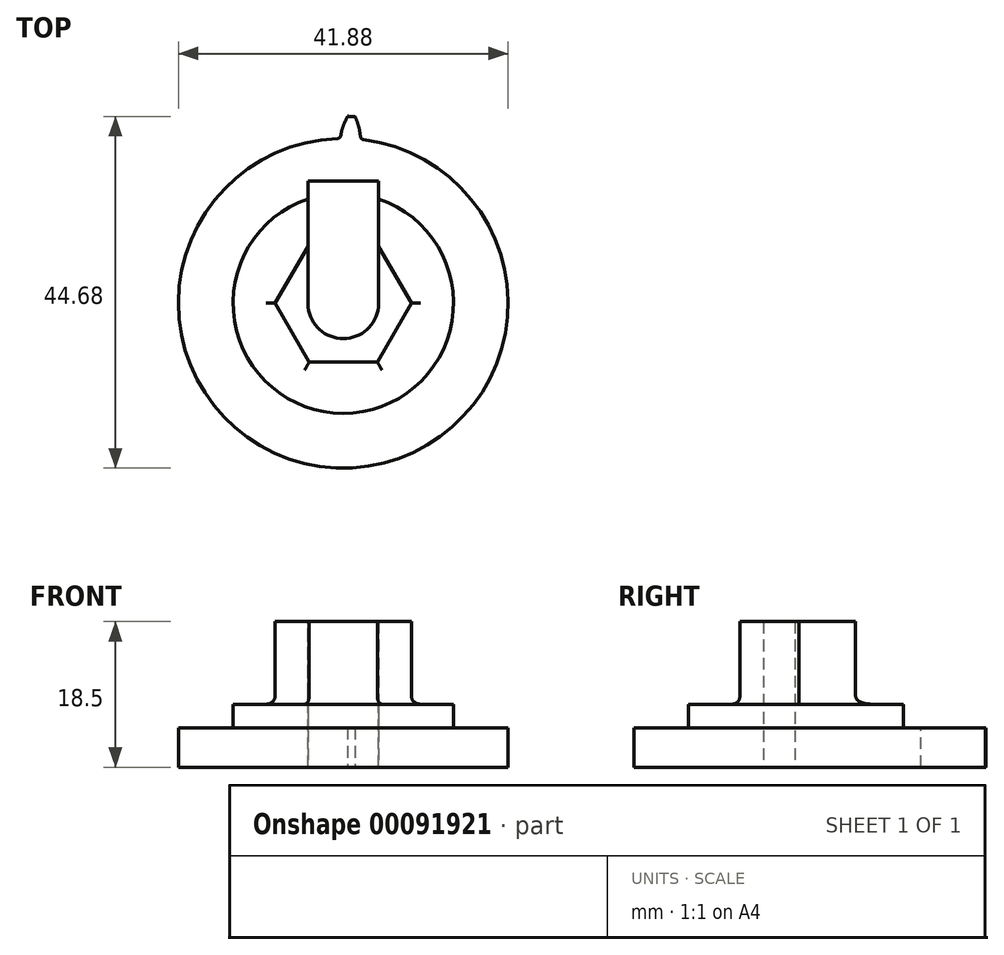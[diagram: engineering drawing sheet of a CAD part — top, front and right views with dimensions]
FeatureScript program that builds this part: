
annotation { "Feature Type Name" : "Feature", "Feature Type Description" : "" }
export const myFeature = defineFeature(function(context is Context, id is Id, definition is map)
    precondition{}
    {
        {
            var Q0;
            Q0=qCreatedBy(makeId("Front.planeOp"),FACE);
            var sketch = newSketch(context, id + "F0", { "sketchPlane" : qUnion([Q0])});
            skLineSegment(sketch, "E0", {"start": v(0, 72.27) * mm, "end": v(0, -50.25) * mm, "construction": true});
            skSolve(sketch);
        }
        {
            var Q0;
            Q0=qCreatedBy(makeId("Top.planeOp"),FACE);
            var sketch = newSketch(context, id + "F1", { "sketchPlane" : qUnion([Q0])});
            skCircle(sketch, "E1", {"center": v(0, 0) * mm, "radius": 22.5 * mm, "construction": true});
            skCircle(sketch, "E2", {"center": v(0, 0) * mm, "radius": 20.94 * mm});
            skCircle(sketch, "E3", {"center": v(0, 0) * mm, "radius": 4.5 * mm});
            skSolve(sketch);
        }
        {
            var Q0;
            Q0=qSketchRegion(id+"F1",true);
            extrude(context, id + "F2", {"entities" : qUnion([Q0]), "depth" : 5 * mm});
        }
        {
            var Q0;
            Q0=qCreatedBy(makeId("Top.planeOp"),FACE);
            var sketch = newSketch(context, id + "F3", { "sketchPlane" : qUnion([Q0])});
            skLineSegment(sketch, "E4", {"start": v(0, 0) * mm, "end": v(0, 29.7) * mm, "construction": true});
            skLineSegment(sketch, "E5", {"start": v(0, 0) * mm, "end": v(-10.47, 28.76) * mm, "construction": true});
            skLineSegment(sketch, "E6", {"start": v(0, 22.5) * mm, "end": v(-7.23, 19.87) * mm, "construction": true});
            skCircle(sketch, "E7", {"center": v(0, 0) * mm, "radius": 22.5 * mm, "construction": true});
            skCircle(sketch, "E8", {"center": v(0, 0) * mm, "radius": 23.75 * mm, "construction": true});
            skArc(sketch, "E9", {"start": v(-0.76, 20.92) * mm, "mid": v(-0.91, -20.92) * mm, "end": v(2.58, 20.78) * mm, "construction": true});
            skCircle(sketch, "E10", {"center": v(0, 0) * mm, "radius": 21.14 * mm, "construction": true});
            skCircle(sketch, "E11", {"center": v(8.83, 19.21) * mm, "radius": 9.42 * mm, "construction": true});
            skCircle(sketch, "E12", {"center": v(5.74, 20.35) * mm, "radius": 6.13 * mm, "construction": true});
            skArc(sketch, "E13", {"start": v(0.57, 23.74) * mm, "mid": v(0.26, 23.13) * mm, "end": v(0, 22.5) * mm});
            skArc(sketch, "E14", {"start": v(0, 22.5) * mm, "mid": v(-0.2, 21.83) * mm, "end": v(-0.34, 21.14) * mm});
            skArc(sketch, "E15", {"start": v(1.96, 22.41) * mm, "mid": v(0.98, 22.48) * mm, "end": v(0, 22.5) * mm});
            skLineSegment(sketch, "E16", {"start": v(0, 0) * mm, "end": v(0.98, 22.48) * mm, "construction": true});
            skLineSegment(sketch, "E17", {"start": v(0.56, 12.86) * mm, "end": v(0.98, 22.48) * mm, "construction": true});
            skArc(sketch, "E18", {"start": v(1.04, 23.73) * mm, "mid": v(0.8, 23.74) * mm, "end": v(0.57, 23.74) * mm});
            skArc(sketch, "E19.MirrorCS", {"start": v(1.04, 23.73) * mm, "mid": v(1.27, 23.72) * mm, "end": v(1.5, 23.7) * mm});
            skArc(sketch, "E20.MirrorCS", {"start": v(1.5, 23.7) * mm, "mid": v(1.76, 23.07) * mm, "end": v(1.96, 22.41) * mm});
            skArc(sketch, "E21.MirrorCS", {"start": v(1.96, 22.41) * mm, "mid": v(2.11, 21.73) * mm, "end": v(2.18, 21.03) * mm});
            skArc(sketch, "E22.filletArc", {"start": v(-0.76, 20.92) * mm, "mid": v(-0.47, 21.04) * mm, "end": v(-0.31, 21.32) * mm});
            skArc(sketch, "E23.MirrorCS", {"start": v(2.58, 20.78) * mm, "mid": v(2.3, 20.92) * mm, "end": v(2.17, 21.2) * mm});
            skArc(sketch, "E24", {"start": v(-0.76, 20.92) * mm, "mid": v(0.91, 20.92) * mm, "end": v(2.58, 20.78) * mm});
            skSolve(sketch);
        }
        {
            var Q0;
            Q0=qSketchRegion(id+"F3",true);
            extrude(context, id + "F4", {"entities" : qUnion([Q0]), "operationType" : NewBodyOperationType.ADD, "depth" : 5 * mm});
        }
        {
            var Q0;
            {var subQ0=sQuery(id+"F3.wireOp",EDGE,"E24");var subQ1=sQuery(id+"F3.wireOp",EDGE,"E23.MirrorCS");var subQ2=sQuery(id+"F3.wireOp",EDGE,"E22.filletArc");var subQ3=sQuery(id+"F3.wireOp",EDGE,"78956dcd-a33f-4312-9058-d5f61c118e150.MirrorCS");var subQ4=sQuery(id+"F3.wireOp",EDGE,"E21.MirrorCS");var subQ5=sQuery(id+"F3.wireOp",EDGE,"E20.MirrorCS");var subQ6=sQuery(id+"F3.wireOp",EDGE,"E19.MirrorCS");var subQ7=sQuery(id+"F3.wireOp",EDGE,"E18");var subQ8=sQuery(id+"F3.wireOp",EDGE,"4TcJw9v4-HVDb-vTLw-8M1V-rvmi7eCVJvvU");var subQ9=sQuery(id+"F3.wireOp",EDGE,"E14");var subQ10=sQuery(id+"F3.wireOp",EDGE,"E13");Q0=makeQuery(id+"FKo0gFQ4KOUnKrD_1.29.F4.boolean.opBoolean","MERGE",FACE,{"derivedFrom":[makeQuery(id+"FKo0gFQ4KOUnKrD_1.28.F4.boolean.opBoolean","MERGE",FACE,{"derivedFrom":[makeQuery(id+"FKo0gFQ4KOUnKrD_1.27.F4.boolean.opBoolean","MERGE",FACE,{"derivedFrom":[makeQuery(id+"FKo0gFQ4KOUnKrD_1.26.F4.boolean.opBoolean","MERGE",FACE,{"derivedFrom":[makeQuery(id+"FKo0gFQ4KOUnKrD_1.25.F4.boolean.opBoolean","MERGE",FACE,{"derivedFrom":[makeQuery(id+"FKo0gFQ4KOUnKrD_1.24.F4.boolean.opBoolean","MERGE",FACE,{"derivedFrom":[makeQuery(id+"FKo0gFQ4KOUnKrD_1.23.F4.boolean.opBoolean","MERGE",FACE,{"derivedFrom":[makeQuery(id+"FKo0gFQ4KOUnKrD_1.22.F4.boolean.opBoolean","MERGE",FACE,{"derivedFrom":[makeQuery(id+"FKo0gFQ4KOUnKrD_1.21.F4.boolean.opBoolean","MERGE",FACE,{"derivedFrom":[makeQuery(id+"FKo0gFQ4KOUnKrD_1.20.F4.boolean.opBoolean","MERGE",FACE,{"derivedFrom":[makeQuery(id+"FKo0gFQ4KOUnKrD_1.19.F4.boolean.opBoolean","MERGE",FACE,{"derivedFrom":[makeQuery(id+"FKo0gFQ4KOUnKrD_1.18.F4.boolean.opBoolean","MERGE",FACE,{"derivedFrom":[makeQuery(id+"FKo0gFQ4KOUnKrD_1.17.F4.boolean.opBoolean","MERGE",FACE,{"derivedFrom":[makeQuery(id+"FKo0gFQ4KOUnKrD_1.16.F4.boolean.opBoolean","MERGE",FACE,{"derivedFrom":[makeQuery(id+"FKo0gFQ4KOUnKrD_1.15.F4.boolean.opBoolean","MERGE",FACE,{"derivedFrom":[makeQuery(id+"FKo0gFQ4KOUnKrD_1.14.F4.boolean.opBoolean","MERGE",FACE,{"derivedFrom":[makeQuery(id+"FKo0gFQ4KOUnKrD_1.13.F4.boolean.opBoolean","MERGE",FACE,{"derivedFrom":[makeQuery(id+"FKo0gFQ4KOUnKrD_1.12.F4.boolean.opBoolean","MERGE",FACE,{"derivedFrom":[makeQuery(id+"FKo0gFQ4KOUnKrD_1.11.F4.boolean.opBoolean","MERGE",FACE,{"derivedFrom":[makeQuery(id+"FKo0gFQ4KOUnKrD_1.10.F4.boolean.opBoolean","MERGE",FACE,{"derivedFrom":[makeQuery(id+"FKo0gFQ4KOUnKrD_1.9.F4.boolean.opBoolean","MERGE",FACE,{"derivedFrom":[makeQuery(id+"FKo0gFQ4KOUnKrD_1.8.F4.boolean.opBoolean","MERGE",FACE,{"derivedFrom":[makeQuery(id+"FKo0gFQ4KOUnKrD_1.7.F4.boolean.opBoolean","MERGE",FACE,{"derivedFrom":[makeQuery(id+"FKo0gFQ4KOUnKrD_1.6.F4.boolean.opBoolean","MERGE",FACE,{"derivedFrom":[makeQuery(id+"FKo0gFQ4KOUnKrD_1.5.F4.boolean.opBoolean","MERGE",FACE,{"derivedFrom":[makeQuery(id+"FKo0gFQ4KOUnKrD_1.4.F4.boolean.opBoolean","MERGE",FACE,{"derivedFrom":[makeQuery(id+"FKo0gFQ4KOUnKrD_1.3.F4.boolean.opBoolean","MERGE",FACE,{"derivedFrom":[makeQuery(id+"FKo0gFQ4KOUnKrD_1.2.F4.boolean.opBoolean","MERGE",FACE,{"derivedFrom":[makeQuery(id+"FKo0gFQ4KOUnKrD_1.1.F4.boolean.opBoolean","MERGE",FACE,{"derivedFrom":[makeQuery(id+"F4.boolean.opBoolean","MERGE",FACE,{"derivedFrom":[makeQuery(id+"F2.opExtrude","CAP_FACE",FACE,{"disambiguationData":[OSD([sQuery(id+"F1.wireOp",EDGE,"E2"),sQuery(id+"F1.wireOp",EDGE,"E3")])],"isStart":false}),makeQuery(id+"F4.opExtrude","CAP_FACE",FACE,{"disambiguationData":[OSD([subQ10,subQ9,subQ8,subQ7,subQ6,subQ5,subQ4,subQ3,subQ2,subQ1,subQ0])],"isStart":false})]}),makeQuery(id+"FKo0gFQ4KOUnKrD_1.1.F4.opExtrude","CAP_FACE",FACE,{"disambiguationData":[OSD([subQ10,subQ9,subQ8,subQ7,subQ6,subQ5,subQ4,subQ3,subQ2,subQ1,subQ0])],"isStart":false})]}),makeQuery(id+"FKo0gFQ4KOUnKrD_1.2.F4.opExtrude","CAP_FACE",FACE,{"disambiguationData":[OSD([subQ10,subQ9,subQ8,subQ7,subQ6,subQ5,subQ4,subQ3,subQ2,subQ1,subQ0])],"isStart":false})]}),makeQuery(id+"FKo0gFQ4KOUnKrD_1.3.F4.opExtrude","CAP_FACE",FACE,{"disambiguationData":[OSD([subQ10,subQ9,subQ8,subQ7,subQ6,subQ5,subQ4,subQ3,subQ2,subQ1,subQ0])],"isStart":false})]}),makeQuery(id+"FKo0gFQ4KOUnKrD_1.4.F4.opExtrude","CAP_FACE",FACE,{"disambiguationData":[OSD([subQ10,subQ9,subQ8,subQ7,subQ6,subQ5,subQ4,subQ3,subQ2,subQ1,subQ0])],"isStart":false})]}),makeQuery(id+"FKo0gFQ4KOUnKrD_1.5.F4.opExtrude","CAP_FACE",FACE,{"disambiguationData":[OSD([subQ10,subQ9,subQ8,subQ7,subQ6,subQ5,subQ4,subQ3,subQ2,subQ1,subQ0])],"isStart":false})]}),makeQuery(id+"FKo0gFQ4KOUnKrD_1.6.F4.opExtrude","CAP_FACE",FACE,{"disambiguationData":[OSD([subQ10,subQ9,subQ8,subQ7,subQ6,subQ5,subQ4,subQ3,subQ2,subQ1,subQ0])],"isStart":false})]}),makeQuery(id+"FKo0gFQ4KOUnKrD_1.7.F4.opExtrude","CAP_FACE",FACE,{"disambiguationData":[OSD([subQ10,subQ9,subQ8,subQ7,subQ6,subQ5,subQ4,subQ3,subQ2,subQ1,subQ0])],"isStart":false})]}),makeQuery(id+"FKo0gFQ4KOUnKrD_1.8.F4.opExtrude","CAP_FACE",FACE,{"disambiguationData":[OSD([subQ10,subQ9,subQ8,subQ7,subQ6,subQ5,subQ4,subQ3,subQ2,subQ1,subQ0])],"isStart":false})]}),makeQuery(id+"FKo0gFQ4KOUnKrD_1.9.F4.opExtrude","CAP_FACE",FACE,{"disambiguationData":[OSD([subQ10,subQ9,subQ8,subQ7,subQ6,subQ5,subQ4,subQ3,subQ2,subQ1,subQ0])],"isStart":false})]}),makeQuery(id+"FKo0gFQ4KOUnKrD_1.10.F4.opExtrude","CAP_FACE",FACE,{"disambiguationData":[OSD([subQ10,subQ9,subQ8,subQ7,subQ6,subQ5,subQ4,subQ3,subQ2,subQ1,subQ0])],"isStart":false})]}),makeQuery(id+"FKo0gFQ4KOUnKrD_1.11.F4.opExtrude","CAP_FACE",FACE,{"disambiguationData":[OSD([subQ10,subQ9,subQ8,subQ7,subQ6,subQ5,subQ4,subQ3,subQ2,subQ1,subQ0])],"isStart":false})]}),makeQuery(id+"FKo0gFQ4KOUnKrD_1.12.F4.opExtrude","CAP_FACE",FACE,{"disambiguationData":[OSD([subQ10,subQ9,subQ8,subQ7,subQ6,subQ5,subQ4,subQ3,subQ2,subQ1,subQ0])],"isStart":false})]}),makeQuery(id+"FKo0gFQ4KOUnKrD_1.13.F4.opExtrude","CAP_FACE",FACE,{"disambiguationData":[OSD([subQ10,subQ9,subQ8,subQ7,subQ6,subQ5,subQ4,subQ3,subQ2,subQ1,subQ0])],"isStart":false})]}),makeQuery(id+"FKo0gFQ4KOUnKrD_1.14.F4.opExtrude","CAP_FACE",FACE,{"disambiguationData":[OSD([subQ10,subQ9,subQ8,subQ7,subQ6,subQ5,subQ4,subQ3,subQ2,subQ1,subQ0])],"isStart":false})]}),makeQuery(id+"FKo0gFQ4KOUnKrD_1.15.F4.opExtrude","CAP_FACE",FACE,{"disambiguationData":[OSD([subQ10,subQ9,subQ8,subQ7,subQ6,subQ5,subQ4,subQ3,subQ2,subQ1,subQ0])],"isStart":false})]}),makeQuery(id+"FKo0gFQ4KOUnKrD_1.16.F4.opExtrude","CAP_FACE",FACE,{"disambiguationData":[OSD([subQ10,subQ9,subQ8,subQ7,subQ6,subQ5,subQ4,subQ3,subQ2,subQ1,subQ0])],"isStart":false})]}),makeQuery(id+"FKo0gFQ4KOUnKrD_1.17.F4.opExtrude","CAP_FACE",FACE,{"disambiguationData":[OSD([subQ10,subQ9,subQ8,subQ7,subQ6,subQ5,subQ4,subQ3,subQ2,subQ1,subQ0])],"isStart":false})]}),makeQuery(id+"FKo0gFQ4KOUnKrD_1.18.F4.opExtrude","CAP_FACE",FACE,{"disambiguationData":[OSD([subQ10,subQ9,subQ8,subQ7,subQ6,subQ5,subQ4,subQ3,subQ2,subQ1,subQ0])],"isStart":false})]}),makeQuery(id+"FKo0gFQ4KOUnKrD_1.19.F4.opExtrude","CAP_FACE",FACE,{"disambiguationData":[OSD([subQ10,subQ9,subQ8,subQ7,subQ6,subQ5,subQ4,subQ3,subQ2,subQ1,subQ0])],"isStart":false})]}),makeQuery(id+"FKo0gFQ4KOUnKrD_1.20.F4.opExtrude","CAP_FACE",FACE,{"disambiguationData":[OSD([subQ10,subQ9,subQ8,subQ7,subQ6,subQ5,subQ4,subQ3,subQ2,subQ1,subQ0])],"isStart":false})]}),makeQuery(id+"FKo0gFQ4KOUnKrD_1.21.F4.opExtrude","CAP_FACE",FACE,{"disambiguationData":[OSD([subQ10,subQ9,subQ8,subQ7,subQ6,subQ5,subQ4,subQ3,subQ2,subQ1,subQ0])],"isStart":false})]}),makeQuery(id+"FKo0gFQ4KOUnKrD_1.22.F4.opExtrude","CAP_FACE",FACE,{"disambiguationData":[OSD([subQ10,subQ9,subQ8,subQ7,subQ6,subQ5,subQ4,subQ3,subQ2,subQ1,subQ0])],"isStart":false})]}),makeQuery(id+"FKo0gFQ4KOUnKrD_1.23.F4.opExtrude","CAP_FACE",FACE,{"disambiguationData":[OSD([subQ10,subQ9,subQ8,subQ7,subQ6,subQ5,subQ4,subQ3,subQ2,subQ1,subQ0])],"isStart":false})]}),makeQuery(id+"FKo0gFQ4KOUnKrD_1.24.F4.opExtrude","CAP_FACE",FACE,{"disambiguationData":[OSD([subQ10,subQ9,subQ8,subQ7,subQ6,subQ5,subQ4,subQ3,subQ2,subQ1,subQ0])],"isStart":false})]}),makeQuery(id+"FKo0gFQ4KOUnKrD_1.25.F4.opExtrude","CAP_FACE",FACE,{"disambiguationData":[OSD([subQ10,subQ9,subQ8,subQ7,subQ6,subQ5,subQ4,subQ3,subQ2,subQ1,subQ0])],"isStart":false})]}),makeQuery(id+"FKo0gFQ4KOUnKrD_1.26.F4.opExtrude","CAP_FACE",FACE,{"disambiguationData":[OSD([subQ10,subQ9,subQ8,subQ7,subQ6,subQ5,subQ4,subQ3,subQ2,subQ1,subQ0])],"isStart":false})]}),makeQuery(id+"FKo0gFQ4KOUnKrD_1.27.F4.opExtrude","CAP_FACE",FACE,{"disambiguationData":[OSD([subQ10,subQ9,subQ8,subQ7,subQ6,subQ5,subQ4,subQ3,subQ2,subQ1,subQ0])],"isStart":false})]}),makeQuery(id+"FKo0gFQ4KOUnKrD_1.28.F4.opExtrude","CAP_FACE",FACE,{"disambiguationData":[OSD([subQ10,subQ9,subQ8,subQ7,subQ6,subQ5,subQ4,subQ3,subQ2,subQ1,subQ0])],"isStart":false})]}),makeQuery(id+"FKo0gFQ4KOUnKrD_1.29.F4.opExtrude","CAP_FACE",FACE,{"disambiguationData":[OSD([subQ10,subQ9,subQ8,subQ7,subQ6,subQ5,subQ4,subQ3,subQ2,subQ1,subQ0])],"isStart":false})]});}
            var sketch = newSketch(context, id + "F5", { "sketchPlane" : qUnion([Q0])});
            skCircle(sketch, "E25.cCircle", {"center": v(0, 0) * mm, "radius": 7.5 * mm, "construction": true});
            skLineSegment(sketch, "E25.0", {"start": v(4.33, 7.5) * mm, "end": v(8.66, 0) * mm});
            skLineSegment(sketch, "E25.1", {"start": v(8.66, 0) * mm, "end": v(4.33, -7.5) * mm});
            skLineSegment(sketch, "E25.2", {"start": v(4.33, -7.5) * mm, "end": v(-4.33, -7.5) * mm});
            skLineSegment(sketch, "E25.3", {"start": v(-4.33, -7.5) * mm, "end": v(-8.66, 0) * mm});
            skLineSegment(sketch, "E25.4", {"start": v(-8.66, 0) * mm, "end": v(-4.33, 7.5) * mm});
            skLineSegment(sketch, "E25.5", {"start": v(-4.33, 7.5) * mm, "end": v(4.33, 7.5) * mm});
            skPoint(sketch, "E25.0.midPoint", {"position": v(6.5, 3.75) * mm});
            skCircle(sketch, "E26.0", {"center": v(0, 0) * mm, "radius": 4.5 * mm});
            skSolve(sketch);
        }
        {
            var Q0;
            Q0 = qSketchRegion(id + "F5", true);
            extrude(context, id + "F6", {"entities" : qUnion([Q0]), "operationType" : NewBodyOperationType.ADD, "depth" : 13.5 * mm});
        }
        {
            var Q0;
            {var subQ0=sQuery(id+"F3.wireOp",EDGE,"E24");var subQ1=sQuery(id+"F3.wireOp",EDGE,"E23.MirrorCS");var subQ2=sQuery(id+"F3.wireOp",EDGE,"E22.filletArc");var subQ3=sQuery(id+"F3.wireOp",EDGE,"E21.MirrorCS");var subQ4=sQuery(id+"F3.wireOp",EDGE,"E20.MirrorCS");var subQ5=sQuery(id+"F3.wireOp",EDGE,"E19.MirrorCS");var subQ6=sQuery(id+"F3.wireOp",EDGE,"E18");var subQ7=sQuery(id+"F3.wireOp",EDGE,"E14");var subQ8=sQuery(id+"F3.wireOp",EDGE,"E13");Q0=makeQuery(id+"FKo0gFQ4KOUnKrD_1.35.F4.boolean.opBoolean","MERGE",FACE,{"derivedFrom":[makeQuery(id+"FKo0gFQ4KOUnKrD_1.34.F4.boolean.opBoolean","MERGE",FACE,{"derivedFrom":[makeQuery(id+"FKo0gFQ4KOUnKrD_1.33.F4.boolean.opBoolean","MERGE",FACE,{"derivedFrom":[makeQuery(id+"FKo0gFQ4KOUnKrD_1.32.F4.boolean.opBoolean","MERGE",FACE,{"derivedFrom":[makeQuery(id+"FKo0gFQ4KOUnKrD_1.31.F4.boolean.opBoolean","MERGE",FACE,{"derivedFrom":[makeQuery(id+"FKo0gFQ4KOUnKrD_1.30.F4.boolean.opBoolean","MERGE",FACE,{"derivedFrom":[makeQuery(id+"FKo0gFQ4KOUnKrD_1.29.F4.boolean.opBoolean","MERGE",FACE,{"derivedFrom":[makeQuery(id+"FKo0gFQ4KOUnKrD_1.28.F4.boolean.opBoolean","MERGE",FACE,{"derivedFrom":[makeQuery(id+"FKo0gFQ4KOUnKrD_1.27.F4.boolean.opBoolean","MERGE",FACE,{"derivedFrom":[makeQuery(id+"FKo0gFQ4KOUnKrD_1.26.F4.boolean.opBoolean","MERGE",FACE,{"derivedFrom":[makeQuery(id+"FKo0gFQ4KOUnKrD_1.25.F4.boolean.opBoolean","MERGE",FACE,{"derivedFrom":[makeQuery(id+"FKo0gFQ4KOUnKrD_1.24.F4.boolean.opBoolean","MERGE",FACE,{"derivedFrom":[makeQuery(id+"FKo0gFQ4KOUnKrD_1.23.F4.boolean.opBoolean","MERGE",FACE,{"derivedFrom":[makeQuery(id+"FKo0gFQ4KOUnKrD_1.22.F4.boolean.opBoolean","MERGE",FACE,{"derivedFrom":[makeQuery(id+"FKo0gFQ4KOUnKrD_1.21.F4.boolean.opBoolean","MERGE",FACE,{"derivedFrom":[makeQuery(id+"FKo0gFQ4KOUnKrD_1.20.F4.boolean.opBoolean","MERGE",FACE,{"derivedFrom":[makeQuery(id+"FKo0gFQ4KOUnKrD_1.19.F4.boolean.opBoolean","MERGE",FACE,{"derivedFrom":[makeQuery(id+"FKo0gFQ4KOUnKrD_1.18.F4.boolean.opBoolean","MERGE",FACE,{"derivedFrom":[makeQuery(id+"FKo0gFQ4KOUnKrD_1.17.F4.boolean.opBoolean","MERGE",FACE,{"derivedFrom":[makeQuery(id+"FKo0gFQ4KOUnKrD_1.16.F4.boolean.opBoolean","MERGE",FACE,{"derivedFrom":[makeQuery(id+"FKo0gFQ4KOUnKrD_1.15.F4.boolean.opBoolean","MERGE",FACE,{"derivedFrom":[makeQuery(id+"FKo0gFQ4KOUnKrD_1.14.F4.boolean.opBoolean","MERGE",FACE,{"derivedFrom":[makeQuery(id+"FKo0gFQ4KOUnKrD_1.13.F4.boolean.opBoolean","MERGE",FACE,{"derivedFrom":[makeQuery(id+"FKo0gFQ4KOUnKrD_1.12.F4.boolean.opBoolean","MERGE",FACE,{"derivedFrom":[makeQuery(id+"FKo0gFQ4KOUnKrD_1.11.F4.boolean.opBoolean","MERGE",FACE,{"derivedFrom":[makeQuery(id+"FKo0gFQ4KOUnKrD_1.10.F4.boolean.opBoolean","MERGE",FACE,{"derivedFrom":[makeQuery(id+"FKo0gFQ4KOUnKrD_1.9.F4.boolean.opBoolean","MERGE",FACE,{"derivedFrom":[makeQuery(id+"FKo0gFQ4KOUnKrD_1.8.F4.boolean.opBoolean","MERGE",FACE,{"derivedFrom":[makeQuery(id+"FKo0gFQ4KOUnKrD_1.7.F4.boolean.opBoolean","MERGE",FACE,{"derivedFrom":[makeQuery(id+"FKo0gFQ4KOUnKrD_1.6.F4.boolean.opBoolean","MERGE",FACE,{"derivedFrom":[makeQuery(id+"FKo0gFQ4KOUnKrD_1.5.F4.boolean.opBoolean","MERGE",FACE,{"derivedFrom":[makeQuery(id+"FKo0gFQ4KOUnKrD_1.4.F4.boolean.opBoolean","MERGE",FACE,{"derivedFrom":[makeQuery(id+"FKo0gFQ4KOUnKrD_1.3.F4.boolean.opBoolean","MERGE",FACE,{"derivedFrom":[makeQuery(id+"FKo0gFQ4KOUnKrD_1.2.F4.boolean.opBoolean","MERGE",FACE,{"derivedFrom":[makeQuery(id+"FKo0gFQ4KOUnKrD_1.1.F4.boolean.opBoolean","MERGE",FACE,{"derivedFrom":[makeQuery(id+"F4.boolean.opBoolean","MERGE",FACE,{"derivedFrom":[makeQuery(id+"F2.opExtrude","CAP_FACE",FACE,{"disambiguationData":[OSD([sQuery(id+"F1.wireOp",EDGE,"E2"),sQuery(id+"F1.wireOp",EDGE,"E3")])],"isStart":false}),makeQuery(id+"F4.opExtrude","CAP_FACE",FACE,{"disambiguationData":[OSD([subQ8,subQ7,subQ6,subQ5,subQ4,subQ3,subQ2,subQ1,subQ0])],"isStart":false})]}),makeQuery(id+"FKo0gFQ4KOUnKrD_1.1.F4.opExtrude","CAP_FACE",FACE,{"disambiguationData":[OSD([subQ8,subQ7,subQ6,subQ5,subQ4,subQ3,subQ2,subQ1,subQ0])],"isStart":false})]}),makeQuery(id+"FKo0gFQ4KOUnKrD_1.2.F4.opExtrude","CAP_FACE",FACE,{"disambiguationData":[OSD([subQ8,subQ7,subQ6,subQ5,subQ4,subQ3,subQ2,subQ1,subQ0])],"isStart":false})]}),makeQuery(id+"FKo0gFQ4KOUnKrD_1.3.F4.opExtrude","CAP_FACE",FACE,{"disambiguationData":[OSD([subQ8,subQ7,subQ6,subQ5,subQ4,subQ3,subQ2,subQ1,subQ0])],"isStart":false})]}),makeQuery(id+"FKo0gFQ4KOUnKrD_1.4.F4.opExtrude","CAP_FACE",FACE,{"disambiguationData":[OSD([subQ8,subQ7,subQ6,subQ5,subQ4,subQ3,subQ2,subQ1,subQ0])],"isStart":false})]}),makeQuery(id+"FKo0gFQ4KOUnKrD_1.5.F4.opExtrude","CAP_FACE",FACE,{"disambiguationData":[OSD([subQ8,subQ7,subQ6,subQ5,subQ4,subQ3,subQ2,subQ1,subQ0])],"isStart":false})]}),makeQuery(id+"FKo0gFQ4KOUnKrD_1.6.F4.opExtrude","CAP_FACE",FACE,{"disambiguationData":[OSD([subQ8,subQ7,subQ6,subQ5,subQ4,subQ3,subQ2,subQ1,subQ0])],"isStart":false})]}),makeQuery(id+"FKo0gFQ4KOUnKrD_1.7.F4.opExtrude","CAP_FACE",FACE,{"disambiguationData":[OSD([subQ8,subQ7,subQ6,subQ5,subQ4,subQ3,subQ2,subQ1,subQ0])],"isStart":false})]}),makeQuery(id+"FKo0gFQ4KOUnKrD_1.8.F4.opExtrude","CAP_FACE",FACE,{"disambiguationData":[OSD([subQ8,subQ7,subQ6,subQ5,subQ4,subQ3,subQ2,subQ1,subQ0])],"isStart":false})]}),makeQuery(id+"FKo0gFQ4KOUnKrD_1.9.F4.opExtrude","CAP_FACE",FACE,{"disambiguationData":[OSD([subQ8,subQ7,subQ6,subQ5,subQ4,subQ3,subQ2,subQ1,subQ0])],"isStart":false})]}),makeQuery(id+"FKo0gFQ4KOUnKrD_1.10.F4.opExtrude","CAP_FACE",FACE,{"disambiguationData":[OSD([subQ8,subQ7,subQ6,subQ5,subQ4,subQ3,subQ2,subQ1,subQ0])],"isStart":false})]}),makeQuery(id+"FKo0gFQ4KOUnKrD_1.11.F4.opExtrude","CAP_FACE",FACE,{"disambiguationData":[OSD([subQ8,subQ7,subQ6,subQ5,subQ4,subQ3,subQ2,subQ1,subQ0])],"isStart":false})]}),makeQuery(id+"FKo0gFQ4KOUnKrD_1.12.F4.opExtrude","CAP_FACE",FACE,{"disambiguationData":[OSD([subQ8,subQ7,subQ6,subQ5,subQ4,subQ3,subQ2,subQ1,subQ0])],"isStart":false})]}),makeQuery(id+"FKo0gFQ4KOUnKrD_1.13.F4.opExtrude","CAP_FACE",FACE,{"disambiguationData":[OSD([subQ8,subQ7,subQ6,subQ5,subQ4,subQ3,subQ2,subQ1,subQ0])],"isStart":false})]}),makeQuery(id+"FKo0gFQ4KOUnKrD_1.14.F4.opExtrude","CAP_FACE",FACE,{"disambiguationData":[OSD([subQ8,subQ7,subQ6,subQ5,subQ4,subQ3,subQ2,subQ1,subQ0])],"isStart":false})]}),makeQuery(id+"FKo0gFQ4KOUnKrD_1.15.F4.opExtrude","CAP_FACE",FACE,{"disambiguationData":[OSD([subQ8,subQ7,subQ6,subQ5,subQ4,subQ3,subQ2,subQ1,subQ0])],"isStart":false})]}),makeQuery(id+"FKo0gFQ4KOUnKrD_1.16.F4.opExtrude","CAP_FACE",FACE,{"disambiguationData":[OSD([subQ8,subQ7,subQ6,subQ5,subQ4,subQ3,subQ2,subQ1,subQ0])],"isStart":false})]}),makeQuery(id+"FKo0gFQ4KOUnKrD_1.17.F4.opExtrude","CAP_FACE",FACE,{"disambiguationData":[OSD([subQ8,subQ7,subQ6,subQ5,subQ4,subQ3,subQ2,subQ1,subQ0])],"isStart":false})]}),makeQuery(id+"FKo0gFQ4KOUnKrD_1.18.F4.opExtrude","CAP_FACE",FACE,{"disambiguationData":[OSD([subQ8,subQ7,subQ6,subQ5,subQ4,subQ3,subQ2,subQ1,subQ0])],"isStart":false})]}),makeQuery(id+"FKo0gFQ4KOUnKrD_1.19.F4.opExtrude","CAP_FACE",FACE,{"disambiguationData":[OSD([subQ8,subQ7,subQ6,subQ5,subQ4,subQ3,subQ2,subQ1,subQ0])],"isStart":false})]}),makeQuery(id+"FKo0gFQ4KOUnKrD_1.20.F4.opExtrude","CAP_FACE",FACE,{"disambiguationData":[OSD([subQ8,subQ7,subQ6,subQ5,subQ4,subQ3,subQ2,subQ1,subQ0])],"isStart":false})]}),makeQuery(id+"FKo0gFQ4KOUnKrD_1.21.F4.opExtrude","CAP_FACE",FACE,{"disambiguationData":[OSD([subQ8,subQ7,subQ6,subQ5,subQ4,subQ3,subQ2,subQ1,subQ0])],"isStart":false})]}),makeQuery(id+"FKo0gFQ4KOUnKrD_1.22.F4.opExtrude","CAP_FACE",FACE,{"disambiguationData":[OSD([subQ8,subQ7,subQ6,subQ5,subQ4,subQ3,subQ2,subQ1,subQ0])],"isStart":false})]}),makeQuery(id+"FKo0gFQ4KOUnKrD_1.23.F4.opExtrude","CAP_FACE",FACE,{"disambiguationData":[OSD([subQ8,subQ7,subQ6,subQ5,subQ4,subQ3,subQ2,subQ1,subQ0])],"isStart":false})]}),makeQuery(id+"FKo0gFQ4KOUnKrD_1.24.F4.opExtrude","CAP_FACE",FACE,{"disambiguationData":[OSD([subQ8,subQ7,subQ6,subQ5,subQ4,subQ3,subQ2,subQ1,subQ0])],"isStart":false})]}),makeQuery(id+"FKo0gFQ4KOUnKrD_1.25.F4.opExtrude","CAP_FACE",FACE,{"disambiguationData":[OSD([subQ8,subQ7,subQ6,subQ5,subQ4,subQ3,subQ2,subQ1,subQ0])],"isStart":false})]}),makeQuery(id+"FKo0gFQ4KOUnKrD_1.26.F4.opExtrude","CAP_FACE",FACE,{"disambiguationData":[OSD([subQ8,subQ7,subQ6,subQ5,subQ4,subQ3,subQ2,subQ1,subQ0])],"isStart":false})]}),makeQuery(id+"FKo0gFQ4KOUnKrD_1.27.F4.opExtrude","CAP_FACE",FACE,{"disambiguationData":[OSD([subQ8,subQ7,subQ6,subQ5,subQ4,subQ3,subQ2,subQ1,subQ0])],"isStart":false})]}),makeQuery(id+"FKo0gFQ4KOUnKrD_1.28.F4.opExtrude","CAP_FACE",FACE,{"disambiguationData":[OSD([subQ8,subQ7,subQ6,subQ5,subQ4,subQ3,subQ2,subQ1,subQ0])],"isStart":false})]}),makeQuery(id+"FKo0gFQ4KOUnKrD_1.29.F4.opExtrude","CAP_FACE",FACE,{"disambiguationData":[OSD([subQ8,subQ7,subQ6,subQ5,subQ4,subQ3,subQ2,subQ1,subQ0])],"isStart":false})]}),makeQuery(id+"FKo0gFQ4KOUnKrD_1.30.F4.opExtrude","CAP_FACE",FACE,{"disambiguationData":[OSD([subQ8,subQ7,subQ6,subQ5,subQ4,subQ3,subQ2,subQ1,subQ0])],"isStart":false})]}),makeQuery(id+"FKo0gFQ4KOUnKrD_1.31.F4.opExtrude","CAP_FACE",FACE,{"disambiguationData":[OSD([subQ8,subQ7,subQ6,subQ5,subQ4,subQ3,subQ2,subQ1,subQ0])],"isStart":false})]}),makeQuery(id+"FKo0gFQ4KOUnKrD_1.32.F4.opExtrude","CAP_FACE",FACE,{"disambiguationData":[OSD([subQ8,subQ7,subQ6,subQ5,subQ4,subQ3,subQ2,subQ1,subQ0])],"isStart":false})]}),makeQuery(id+"FKo0gFQ4KOUnKrD_1.33.F4.opExtrude","CAP_FACE",FACE,{"disambiguationData":[OSD([subQ8,subQ7,subQ6,subQ5,subQ4,subQ3,subQ2,subQ1,subQ0])],"isStart":false})]}),makeQuery(id+"FKo0gFQ4KOUnKrD_1.34.F4.opExtrude","CAP_FACE",FACE,{"disambiguationData":[OSD([subQ8,subQ7,subQ6,subQ5,subQ4,subQ3,subQ2,subQ1,subQ0])],"isStart":false})]}),makeQuery(id+"FKo0gFQ4KOUnKrD_1.35.F4.opExtrude","CAP_FACE",FACE,{"disambiguationData":[OSD([subQ8,subQ7,subQ6,subQ5,subQ4,subQ3,subQ2,subQ1,subQ0])],"isStart":false})]});}
            var sketch = newSketch(context, id + "F7", { "sketchPlane" : qUnion([Q0])});
            skCircle(sketch, "E27", {"center": v(0, 0) * mm, "radius": 14 * mm});
            skCircle(sketch, "E28", {"center": v(0, 0) * mm, "radius": 4.5 * mm});
            skSolve(sketch);
        }
        {
            var Q0;
            Q0 = qSketchRegion(id + "F7", true);
            extrude(context, id + "F8", {"entities" : qUnion([Q0]), "operationType" : NewBodyOperationType.ADD, "depth" : 3 * mm});
        }
        {
            var Q0;
            Q0=makeQuery(id+"F6.opExtrude","CAP_FACE",FACE,{"disambiguationData":[OSD([sQuery(id+"F5.wireOp",EDGE,"E25.0"),sQuery(id+"F5.wireOp",EDGE,"E25.1"),sQuery(id+"F5.wireOp",EDGE,"E25.2"),sQuery(id+"F5.wireOp",EDGE,"E25.3"),sQuery(id+"F5.wireOp",EDGE,"E25.4"),sQuery(id+"F5.wireOp",EDGE,"E25.5"),sQuery(id+"F5.wireOp",EDGE,"E26.0")])],"isStart":false});
            var sketch = newSketch(context, id + "F9", { "sketchPlane" : qUnion([Q0])});
            skLineSegment(sketch, "E29.bottom", {"start": v(4.5, 15.5) * mm, "end": v(-4.5, 15.5) * mm});
            skLineSegment(sketch, "E29.top", {"start": v(4.5, -0.5) * mm, "end": v(-4.5, -0.5) * mm});
            skLineSegment(sketch, "E29.left", {"start": v(4.5, 15.5) * mm, "end": v(4.5, -0.5) * mm});
            skLineSegment(sketch, "E29.right", {"start": v(-4.5, 15.5) * mm, "end": v(-4.5, -0.5) * mm});
            skPoint(sketch, "E29.middle", {"position": v(0, 7.5) * mm});
            skSolve(sketch);
        }
        {
            var Q0;
            Q0 = qSketchRegion(id + "F9", true);
            extrude(context, id + "F10", {"entities" : qUnion([Q0]), "operationType" : NewBodyOperationType.REMOVE, "endBound" : BoundingType.THROUGH_ALL, "oppositeDirection" : true, "depth" : 25 * mm});
        }
        {
            var Q0;
            Q0=makeQuery(id+"F8.boolean.opBoolean","INTERSECT",EDGE,{"derivedFrom":[makeQuery(id+"F6.opExtrude","SWEPT_FACE",FACE,{"disambiguationData":[OSD([sQuery(id+"F5.wireOp",EDGE,"E25.3")])]}),makeQuery(id+"F8.opExtrude","CAP_FACE",FACE,{"disambiguationData":[OSD([sQuery(id+"F7.wireOp",EDGE,"E27"),sQuery(id+"F7.wireOp",EDGE,"E28")])],"isStart":false})]});
            var Q1;
            Q1=makeQuery(id+"F8.boolean.opBoolean","INTERSECT",EDGE,{"derivedFrom":[makeQuery(id+"F6.opExtrude","SWEPT_FACE",FACE,{"disambiguationData":[OSD([sQuery(id+"F5.wireOp",EDGE,"E25.1")])]}),makeQuery(id+"F8.opExtrude","CAP_FACE",FACE,{"disambiguationData":[OSD([sQuery(id+"F7.wireOp",EDGE,"E27"),sQuery(id+"F7.wireOp",EDGE,"E28")])],"isStart":false})]});
            var Q2;
            Q2=makeQuery(id+"F8.boolean.opBoolean","INTERSECT",EDGE,{"derivedFrom":[makeQuery(id+"F6.opExtrude","SWEPT_FACE",FACE,{"disambiguationData":[OSD([sQuery(id+"F5.wireOp",EDGE,"E25.4")])]}),makeQuery(id+"F8.opExtrude","CAP_FACE",FACE,{"disambiguationData":[OSD([sQuery(id+"F7.wireOp",EDGE,"E27"),sQuery(id+"F7.wireOp",EDGE,"E28")])],"isStart":false})]});
            var Q3;
            Q3=makeQuery(id+"F8.boolean.opBoolean","INTERSECT",EDGE,{"derivedFrom":[makeQuery(id+"F6.opExtrude","SWEPT_FACE",FACE,{"disambiguationData":[OSD([sQuery(id+"F5.wireOp",EDGE,"E25.0")])]}),makeQuery(id+"F8.opExtrude","CAP_FACE",FACE,{"disambiguationData":[OSD([sQuery(id+"F7.wireOp",EDGE,"E27"),sQuery(id+"F7.wireOp",EDGE,"E28")])],"isStart":false})]});
            var Q4;
            Q4=makeQuery(id+"F8.opExtrude","CAP_EDGE",EDGE,{"disambiguationData":[OSD([sQuery(id+"F7.wireOp",EDGE,"E27")])],"isStart":true});
            var Q5;
            Q5=makeQuery(id+"F8.boolean.opBoolean","INTERSECT",EDGE,{"derivedFrom":[makeQuery(id+"F6.opExtrude","SWEPT_FACE",FACE,{"disambiguationData":[OSD([sQuery(id+"F5.wireOp",EDGE,"E25.2")])]}),makeQuery(id+"F8.opExtrude","CAP_FACE",FACE,{"disambiguationData":[OSD([sQuery(id+"F7.wireOp",EDGE,"E27"),sQuery(id+"F7.wireOp",EDGE,"E28")])],"isStart":false})]});
            fillet(context, id + "F11", {"entities" : qUnion([Q0, Q1, Q2, Q3, Q4, Q5]), "radius" : 1 * mm, "tangentPropagation" : true, "allowEdgeOverflow" : false});
        }
    });
